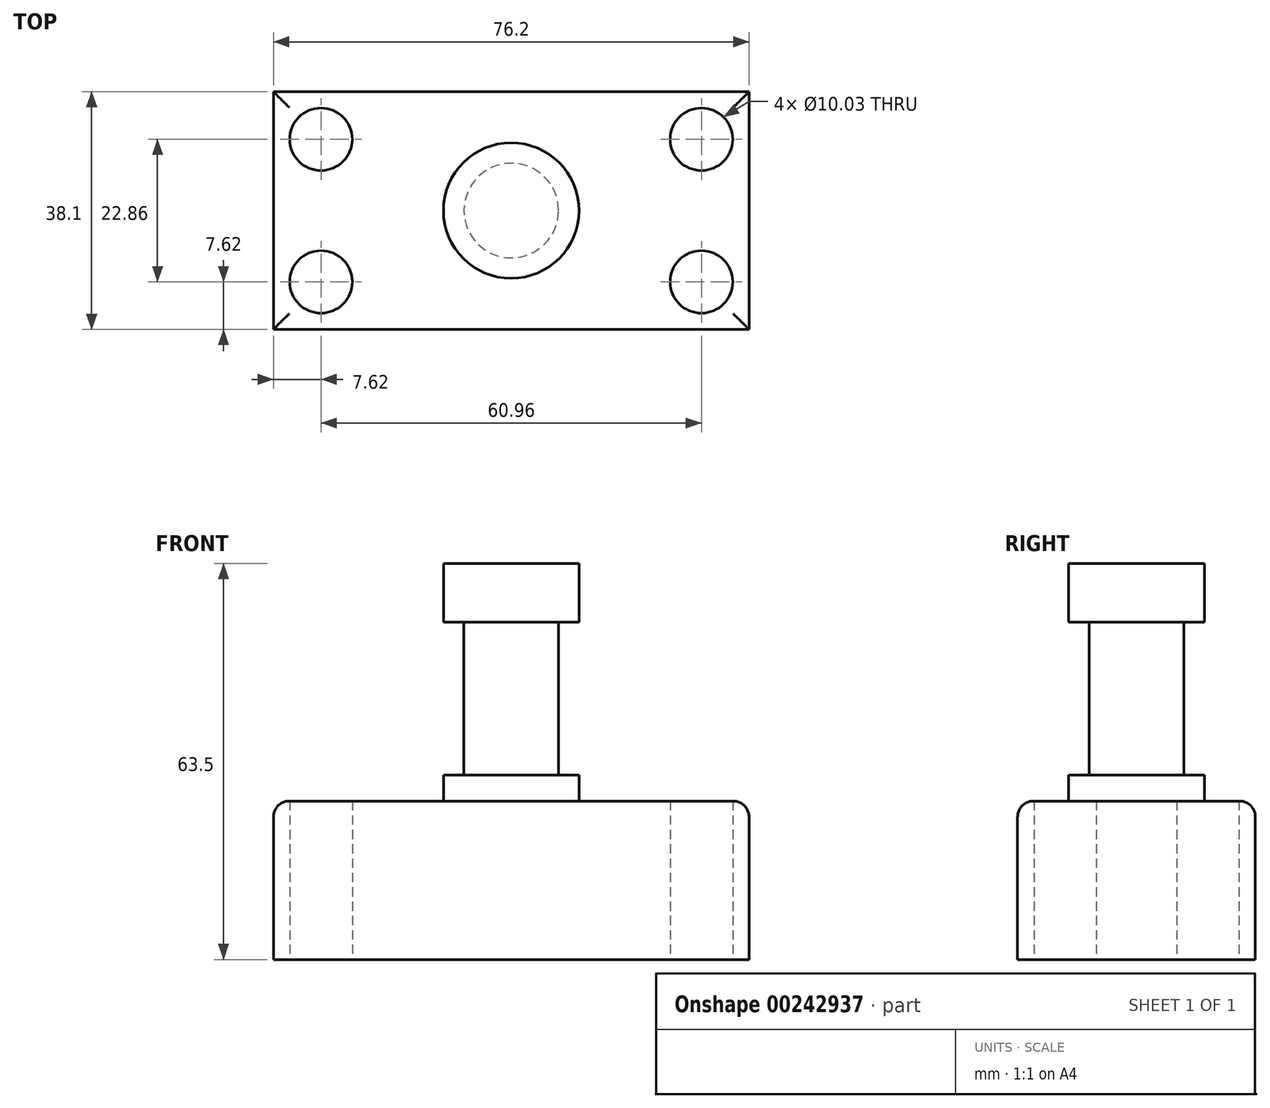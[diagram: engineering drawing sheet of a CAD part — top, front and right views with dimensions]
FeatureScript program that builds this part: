
annotation { "Feature Type Name" : "Feature", "Feature Type Description" : "" }
export const myFeature = defineFeature(function(context is Context, id is Id, definition is map)
    precondition{}
    {
        {
            var Q0;
            Q0=qCreatedBy(makeId("Top.planeOp"),FACE);
            var sketch = newSketch(context, id + "F0", { "sketchPlane" : qUnion([Q0])});
            skLineSegment(sketch, "E0.bottom", {"start": v(-38.1, 19.05) * mm, "end": v(38.1, 19.05) * mm});
            skLineSegment(sketch, "E0.top", {"start": v(-38.1, -19.05) * mm, "end": v(38.1, -19.05) * mm});
            skLineSegment(sketch, "E0.left", {"start": v(-38.1, 19.05) * mm, "end": v(-38.1, -19.05) * mm});
            skLineSegment(sketch, "E0.right", {"start": v(38.1, 19.05) * mm, "end": v(38.1, -19.05) * mm});
            skPoint(sketch, "E0.middle", {"position": v(0, 0) * mm});
            skSolve(sketch);
        }
        {
            var Q0;
            Q0 = qSketchRegion(id + "F0", true);
            extrude(context, id + "F1", {"entities" : qUnion([Q0]), "depth" : 25.4 * mm});
        }
        {
            var Q0;
            Q0=qCreatedBy(makeId("Top.planeOp"),FACE);
            var sketch = newSketch(context, id + "F2", { "sketchPlane" : qUnion([Q0])});
            skCircle(sketch, "E1", {"center": v(-30.48, -11.43) * mm, "radius": 5.01 * mm});
            skCircle(sketch, "E2", {"center": v(30.48, -11.43) * mm, "radius": 5.01 * mm});
            skCircle(sketch, "E3", {"center": v(30.48, 11.43) * mm, "radius": 5.01 * mm});
            skCircle(sketch, "E4", {"center": v(-30.48, 11.43) * mm, "radius": 5.01 * mm});
            skSolve(sketch);
        }
        {
            var Q0;
            Q0 = qSketchRegion(id + "F2", true);
            extrude(context, id + "F3", {"entities" : qUnion([Q0]), "operationType" : NewBodyOperationType.REMOVE, "depth" : 25.4 * mm});
        }
        {
            var Q0;
            Q0=makeQuery(id+"F1.opExtrude","CAP_FACE",FACE,{"disambiguationData":[OSD([sQuery(id+"F0.wireOp",EDGE,"E0.bottom"),sQuery(id+"F0.wireOp",EDGE,"E0.top"),sQuery(id+"F0.wireOp",EDGE,"E0.left"),sQuery(id+"F0.wireOp",EDGE,"E0.right")])],"isStart":false});
            var sketch = newSketch(context, id + "F4", { "sketchPlane" : qUnion([Q0])});
            skCircle(sketch, "E5", {"center": v(0, 0) * mm, "radius": 10.86 * mm});
            skSolve(sketch);
        }
        {
            var Q0;
            Q0 = qSketchRegion(id + "F4", true);
            extrude(context, id + "F5", {"entities" : qUnion([Q0]), "operationType" : NewBodyOperationType.ADD, "depth" : 38.1 * mm});
        }
        {
            var Q0;
            Q0=makeQuery(id+"F1.opExtrude","CAP_EDGE",EDGE,{"disambiguationData":[OSD([sQuery(id+"F0.wireOp",EDGE,"E0.bottom")])],"isStart":false});
            var Q1;
            Q1=makeQuery(id+"F1.opExtrude","CAP_EDGE",EDGE,{"disambiguationData":[OSD([sQuery(id+"F0.wireOp",EDGE,"E0.left")])],"isStart":false});
            var Q2;
            Q2=makeQuery(id+"F1.opExtrude","CAP_EDGE",EDGE,{"disambiguationData":[OSD([sQuery(id+"F0.wireOp",EDGE,"E0.top")])],"isStart":false});
            var Q3;
            Q3=makeQuery(id+"F1.opExtrude","CAP_EDGE",EDGE,{"disambiguationData":[OSD([sQuery(id+"F0.wireOp",EDGE,"E0.right")])],"isStart":false});
            fillet(context, id + "F6", {"entities" : qUnion([Q0, Q1, Q2, Q3]), "radius" : 2.54 * mm, "tangentPropagation" : true, "allowEdgeOverflow" : false});
        }
        {
            var Q0;
            Q0=qCreatedBy(makeId("Front.planeOp"),FACE);
            var sketch = newSketch(context, id + "F7", { "sketchPlane" : qUnion([Q0])});
            skLineSegment(sketch, "E6.bottom", {"start": v(7.58, 29.58) * mm, "end": v(26.23, 29.58) * mm});
            skLineSegment(sketch, "E6.top", {"start": v(7.58, 54.07) * mm, "end": v(26.23, 54.07) * mm});
            skLineSegment(sketch, "E6.left", {"start": v(7.58, 29.58) * mm, "end": v(7.58, 54.07) * mm});
            skLineSegment(sketch, "E6.right", {"start": v(26.23, 29.58) * mm, "end": v(26.23, 54.07) * mm});
            skPoint(sketch, "E6.middle", {"position": v(16.9, 41.83) * mm});
            skSolve(sketch);
        }
        {
            var Q0;
            Q0 = qSketchRegion(id + "F7", true);
            var Q1;
            Q1=makeQuery(id+"F5.opExtrude","SWEPT_FACE",FACE,{"disambiguationData":[OSD([sQuery(id+"F4.wireOp",EDGE,"E5")])]});
            revolve(context, id + "F8", {"operationType" : NewBodyOperationType.REMOVE, "entities" : qUnion([Q0]), "axis" : qUnion([Q1]), "revolveType" : RevolveType.FULL, "oppositeDirection" : true});
        }
    });
